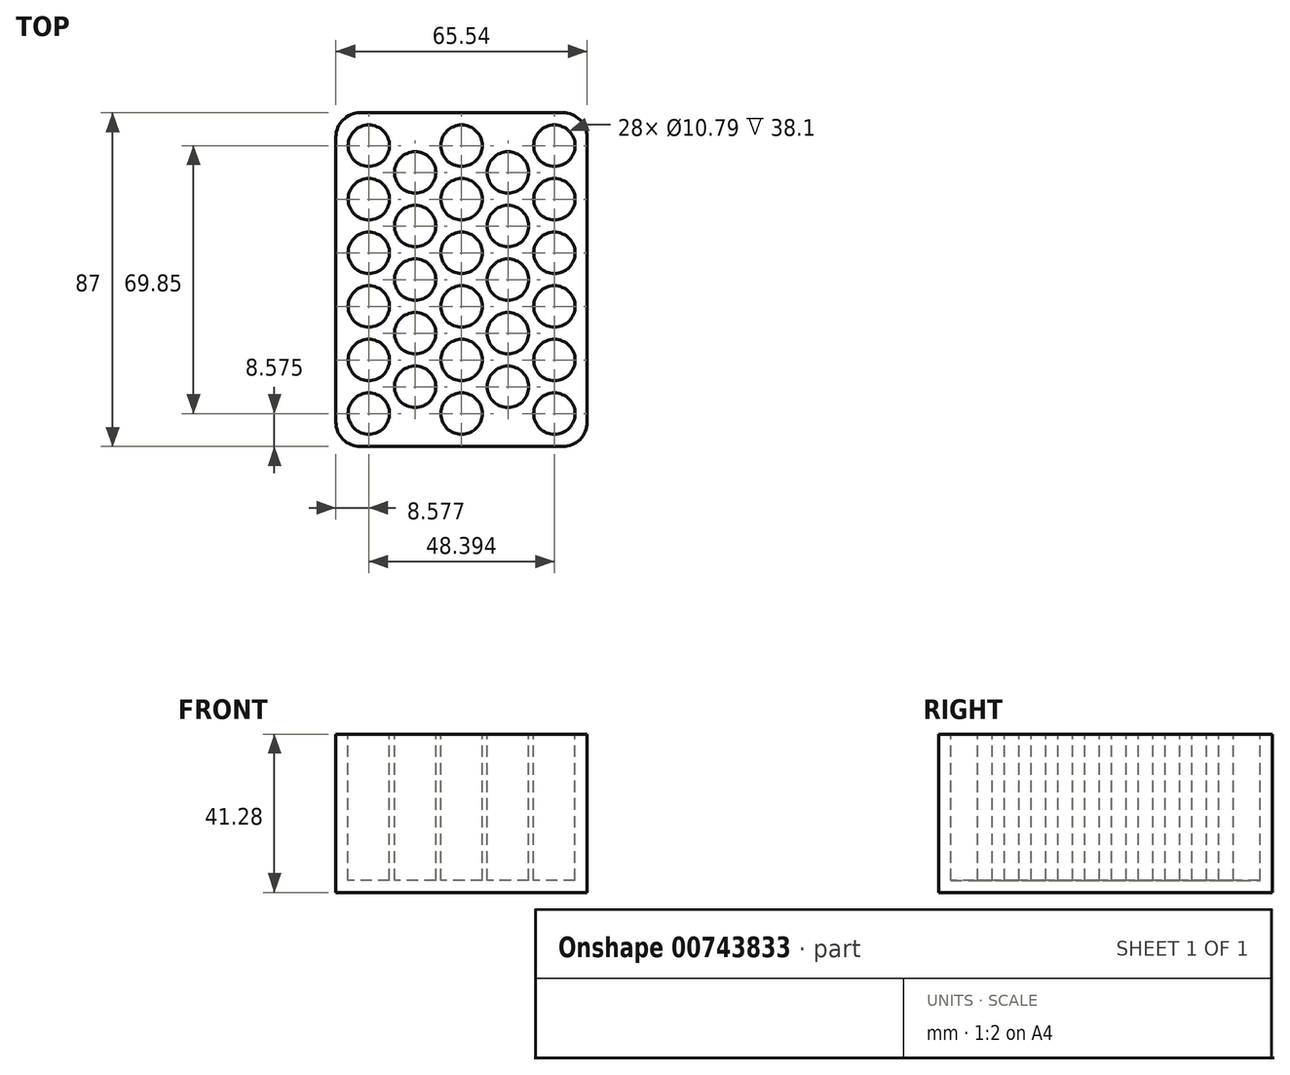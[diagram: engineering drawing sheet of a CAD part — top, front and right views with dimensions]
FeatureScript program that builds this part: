
annotation { "Feature Type Name" : "Feature", "Feature Type Description" : "" }
export const myFeature = defineFeature(function(context is Context, id is Id, definition is map)
    precondition{}
    {
        {
            var Q0;
            Q0=qCreatedBy(makeId("Top.planeOp"),FACE);
            var sketch = newSketch(context, id + "F0", { "sketchPlane" : qUnion([Q0])});
            skLineSegment(sketch, "E0.bottom", {"start": v(-32.77, 43.5) * mm, "end": v(32.77, 43.5) * mm});
            skLineSegment(sketch, "E0.top", {"start": v(-32.77, -43.5) * mm, "end": v(32.77, -43.5) * mm});
            skLineSegment(sketch, "E0.left", {"start": v(-32.77, 43.5) * mm, "end": v(-32.77, -43.5) * mm});
            skLineSegment(sketch, "E0.right", {"start": v(32.77, 43.5) * mm, "end": v(32.77, -43.5) * mm});
            skLineSegment(sketch, "E1", {"start": v(0, 43.5) * mm, "end": v(0, 0) * mm, "construction": true});
            skLineSegment(sketch, "E2", {"start": v(0, 0) * mm, "end": v(-32.77, 0) * mm, "construction": true});
            skSolve(sketch);
        }
        {
            var Q0;
            Q0 = qSketchRegion(id + "F0", true);
            extrude(context, id + "F1", {"entities" : qUnion([Q0]), "depth" : 41.27 * mm, "offsetDistance" : 25.4 * mm});
        }
        {
            var Q0;
            Q0=makeQuery(id+"F1.opExtrude","CAP_FACE",FACE,{"disambiguationData":[OSD([sQuery(id+"F0.wireOp",EDGE,"E0.bottom"),sQuery(id+"F0.wireOp",EDGE,"E0.top"),sQuery(id+"F0.wireOp",EDGE,"E0.left"),sQuery(id+"F0.wireOp",EDGE,"E0.right")])],"isStart":false});
            var sketch = newSketch(context, id + "F2", { "sketchPlane" : qUnion([Q0])});
            skCircle(sketch, "E3", {"center": v(-24.2, 34.92) * mm, "radius": 5.4 * mm});
            skCircle(sketch, "E4.1.0.0", {"center": v(-24.2, 20.95) * mm, "radius": 5.4 * mm});
            skCircle(sketch, "E4.2.0.0", {"center": v(-24.2, 6.98) * mm, "radius": 5.4 * mm});
            skLineSegment(sketch, "E4.direction1", {"start": v(-24.2, 34.92) * mm, "end": v(-24.2, 20.95) * mm, "construction": true});
            skCircle(sketch, "E5.0.3.0", {"center": v(-24.2, -6.99) * mm, "radius": 5.4 * mm});
            skCircle(sketch, "E5.0.4.0", {"center": v(-24.2, -20.96) * mm, "radius": 5.4 * mm});
            skCircle(sketch, "E6.0.5.0", {"center": v(-24.2, -34.93) * mm, "radius": 5.4 * mm});
            skCircle(sketch, "E7", {"center": v(-12.1, 27.94) * mm, "radius": 5.4 * mm});
            skLineSegment(sketch, "E8", {"start": v(-12.1, 27.94) * mm, "end": v(-24.2, 34.93) * mm, "construction": true});
            skLineSegment(sketch, "E9", {"start": v(-24.2, 20.95) * mm, "end": v(-12.1, 27.94) * mm, "construction": true});
            skCircle(sketch, "E10.1.0.0", {"center": v(-12.1, 13.97) * mm, "radius": 5.4 * mm});
            skCircle(sketch, "E10.2.0.0", {"center": v(-12.1, 0) * mm, "radius": 5.4 * mm});
            skLineSegment(sketch, "E10.direction1", {"start": v(-12.1, 27.94) * mm, "end": v(-12.1, 13.97) * mm, "construction": true});
            skCircle(sketch, "E11.0.3.0", {"center": v(-12.1, -13.97) * mm, "radius": 5.4 * mm});
            skCircle(sketch, "E11.0.4.0", {"center": v(-12.1, -27.94) * mm, "radius": 5.4 * mm});
            skLineSegment(sketch, "E12.1.0.0", {"start": v(12.1, 27.94) * mm, "end": v(12.1, 13.97) * mm, "construction": true});
            skCircle(sketch, "E12.1.0.1", {"center": v(12.1, 0) * mm, "radius": 5.4 * mm});
            skLineSegment(sketch, "E12.1.0.2", {"start": v(0, 34.92) * mm, "end": v(0, 20.95) * mm, "construction": true});
            skCircle(sketch, "E12.1.0.3", {"center": v(12.1, 13.97) * mm, "radius": 5.4 * mm});
            skLineSegment(sketch, "E12.1.0.4", {"start": v(0, 20.95) * mm, "end": v(12.1, 27.94) * mm, "construction": true});
            skCircle(sketch, "E12.1.0.5", {"center": v(12.1, -13.97) * mm, "radius": 5.4 * mm});
            skCircle(sketch, "E12.1.0.6", {"center": v(0, 6.98) * mm, "radius": 5.4 * mm});
            skCircle(sketch, "E12.1.0.7", {"center": v(0, 20.95) * mm, "radius": 5.4 * mm});
            skCircle(sketch, "E12.1.0.8", {"center": v(0, 34.92) * mm, "radius": 5.4 * mm});
            skCircle(sketch, "E12.1.0.9", {"center": v(12.1, -27.94) * mm, "radius": 5.4 * mm});
            skLineSegment(sketch, "E12.1.0.10", {"start": v(12.1, 27.94) * mm, "end": v(0, 34.93) * mm, "construction": true});
            skCircle(sketch, "E12.1.0.11", {"center": v(12.1, 27.94) * mm, "radius": 5.4 * mm});
            skCircle(sketch, "E12.1.0.12", {"center": v(0, -6.99) * mm, "radius": 5.4 * mm});
            skCircle(sketch, "E12.1.0.13", {"center": v(0, -20.96) * mm, "radius": 5.4 * mm});
            skCircle(sketch, "E12.1.0.14", {"center": v(0, -34.93) * mm, "radius": 5.4 * mm});
            skLineSegment(sketch, "E12.2.0.2", {"start": v(24.2, 34.92) * mm, "end": v(24.2, 20.95) * mm, "construction": true});
            skCircle(sketch, "E12.2.0.6", {"center": v(24.2, 6.98) * mm, "radius": 5.4 * mm});
            skCircle(sketch, "E12.2.0.7", {"center": v(24.2, 20.95) * mm, "radius": 5.4 * mm});
            skCircle(sketch, "E12.2.0.8", {"center": v(24.2, 34.92) * mm, "radius": 5.4 * mm});
            skLineSegment(sketch, "E12.2.0.10", {"start": v(36.3, 27.94) * mm, "end": v(24.2, 34.93) * mm, "construction": true});
            skCircle(sketch, "E12.2.0.12", {"center": v(24.2, -6.99) * mm, "radius": 5.4 * mm});
            skCircle(sketch, "E12.2.0.13", {"center": v(24.2, -20.96) * mm, "radius": 5.4 * mm});
            skCircle(sketch, "E12.2.0.14", {"center": v(24.2, -34.93) * mm, "radius": 5.4 * mm});
            skLineSegment(sketch, "E12.direction1", {"start": v(-24.2, -34.93) * mm, "end": v(0, -34.93) * mm, "construction": true});
            skSolve(sketch);
        }
        {
            var Q0;
            Q0 = qSketchRegion(id + "F2", true);
            extrude(context, id + "F3", {"entities" : qUnion([Q0]), "operationType" : NewBodyOperationType.REMOVE, "oppositeDirection" : true, "depth" : 38.1 * mm, "offsetDistance" : 25.4 * mm});
        }
        {
            var Q0;
            Q0=makeQuery(id+"F1.opExtrude","SWEPT_EDGE",EDGE,{"disambiguationData":[OSD([sQuery(id+"F0.wireOp",EDGE,"E0.top"),sQuery(id+"F0.wireOp",EDGE,"E0.left")])]});
            var Q1;
            Q1=makeQuery(id+"F1.opExtrude","SWEPT_EDGE",EDGE,{"disambiguationData":[OSD([sQuery(id+"F0.wireOp",EDGE,"E0.top"),sQuery(id+"F0.wireOp",EDGE,"E0.right")])]});
            var Q2;
            Q2=makeQuery(id+"F1.opExtrude","SWEPT_EDGE",EDGE,{"disambiguationData":[OSD([sQuery(id+"F0.wireOp",EDGE,"E0.bottom"),sQuery(id+"F0.wireOp",EDGE,"E0.right")])]});
            var Q3;
            Q3=makeQuery(id+"F1.opExtrude","SWEPT_EDGE",EDGE,{"disambiguationData":[OSD([sQuery(id+"F0.wireOp",EDGE,"E0.bottom"),sQuery(id+"F0.wireOp",EDGE,"E0.left")])]});
            fillet(context, id + "F4", {"entities" : qUnion([Q0, Q1, Q2, Q3]), "radius" : 6.35 * mm, "tangentPropagation" : true, "allowEdgeOverflow" : false});
        }
    });
